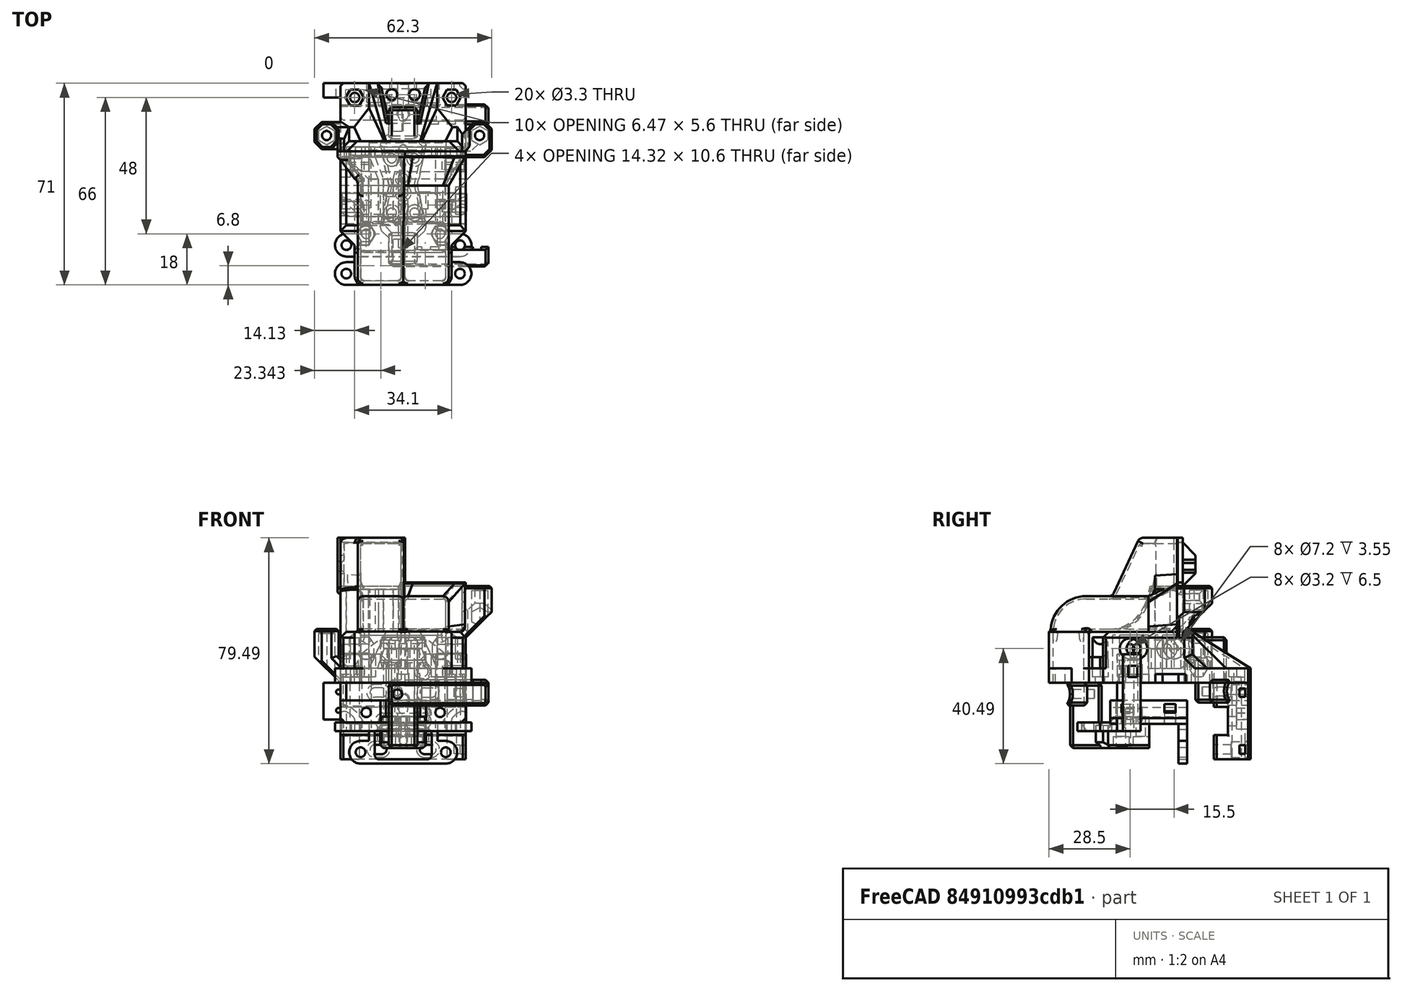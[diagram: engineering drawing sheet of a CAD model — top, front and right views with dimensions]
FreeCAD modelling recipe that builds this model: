
FCSTD DOCUMENT  (FreeCAD 0.19R24291 (Git))
Label: mounting-plate-dual-5015
License: Other
LicenseURL: GPL3
objects: Part::Box×16, Part::Cylinder×13, Part::MultiFuse×12, Part::Feature×11, Part::Cut×10, Part::Chamfer×3, Part::MultiCommon×1
note: 66 computed .brp shape members not serialized (recipe doc carries the construction recipe); baked Part::Feature solids carry a one-line shape summary decoded from their .brp

FEATURE [Part::Cylinder] Cylinder013
  Angle = 360
  AttacherType = Attacher::AttachEngine3D
  Height = 44
  Placement = pos=(21.5,6.5,13.5) rot=(0.707107,0,-0.707107;3.14159rad)
  Radius = 1.6
FEATURE [Part::Cylinder] Cylinder014
  Angle = 360
  AttacherType = Attacher::AttachEngine3D
  Height = 44
  Placement = pos=(-21.5,-6.5,13.5) rot=(0,1,0;1.5708rad)
  Radius = 1.6
FEATURE [Part::Cylinder] Cylinder015
  Angle = 360
  AttacherType = Attacher::AttachEngine3D
  Height = 4
  Placement = pos=(18.5,-6.5,13.5) rot=(0,1,0;1.5708rad)
  Radius = 3.6
FEATURE [Part::Cylinder] Cylinder016
  Angle = 360
  AttacherType = Attacher::AttachEngine3D
  Height = 4
  Placement = pos=(-18.5,6.5,13.5) rot=(0.707107,0,-0.707107;3.14159rad)
  Radius = 3.6
FEATURE [Part::Box] Box012  label="belt-slot"
  AttacherType = Attacher::AttachEngine3D
  Height = 10.2
  Length = 27
  Placement = pos=(-12,15.1,3.5) rot=(1,0,0;1.5708rad)
  Width = 16.7
FEATURE [Part::Box] Box013  label="belt-slot003"
  AttacherType = Attacher::AttachEngine3D
  Height = 10.2
  Length = 27
  Placement = pos=(-15,0.1,3.5) rot=(1,0,0;1.5708rad)
  Width = 16.7
FEATURE [Part::MultiFuse] Fusion001007010
  Placement = pos=(0,2.5,2) rot=(0,0,1;0rad)
  Shapes = -> [Cylinder015,Cylinder016,Cylinder013,Cylinder014]
FEATURE [Part::Box] Box022  label="Cube020"
  AttacherType = Attacher::AttachEngine3D
  Height = 3
  Length = 10
  Placement = pos=(13,4.9,3.5) rot=(0,0,1;0rad)
  Width = 8.2
FEATURE [Part::Box] Box023  label="Cube021"
  AttacherType = Attacher::AttachEngine3D
  Height = 3
  Length = 10
  Placement = pos=(-23,-8.1,3.5) rot=(0,0,1;0rad)
  Width = 8.2
FEATURE [Part::MultiFuse] Fusion001007011023
  Shapes = -> [Box023,Box022]
FEATURE [Part::Cylinder] Cylinder019
  Angle = 360
  AttacherType = Attacher::AttachEngine3D
  Height = 4
  Placement = pos=(-18.5,6.5,13.5) rot=(0.707107,0,-0.707107;3.14159rad)
  Radius = 3.6
FEATURE [Part::Box] Box024  label="belt-slot004"
  AttacherType = Attacher::AttachEngine3D
  Height = 10.2
  Length = 27
  Placement = pos=(-12,12.6,3.5) rot=(1,0,0;1.5708rad)
  Width = 16.7
FEATURE [Part::Box] Box025  label="belt-slot005"
  AttacherType = Attacher::AttachEngine3D
  Height = 10.2
  Length = 27
  Placement = pos=(-15,-2.4,3.5) rot=(1,0,0;1.5708rad)
  Width = 16.7
FEATURE [Part::Cylinder] Cylinder020
  Angle = 360
  AttacherType = Attacher::AttachEngine3D
  Height = 44
  Placement = pos=(21.5,6.5,13.5) rot=(0.707107,0,-0.707107;3.14159rad)
  Radius = 1.6
FEATURE [Part::Cylinder] Cylinder021
  Angle = 360
  AttacherType = Attacher::AttachEngine3D
  Height = 44
  Placement = pos=(-21.5,-6.5,13.5) rot=(0,1,0;1.5708rad)
  Radius = 1.6
FEATURE [Part::Cylinder] Cylinder022
  Angle = 360
  AttacherType = Attacher::AttachEngine3D
  Height = 4
  Placement = pos=(18.5,-6.5,13.5) rot=(0,1,0;1.5708rad)
  Radius = 3.6
FEATURE [Part::MultiFuse] Fusion001007011029
  Placement = pos=(0,0,2) rot=(0,0,1;0rad)
  Shapes = -> [Cylinder022,Cylinder019,Cylinder020,Cylinder021]
FEATURE [Part::Box] Box027  label="Cube023"
  AttacherType = Attacher::AttachEngine3D
  Height = 3
  Length = 10
  Placement = pos=(13,4.9,3.5) rot=(0,0,1;0rad)
  Width = 8.2
FEATURE [Part::Box] Box028  label="Cube024"
  AttacherType = Attacher::AttachEngine3D
  Height = 3
  Length = 10
  Placement = pos=(-23,-8.1,3.5) rot=(0,0,1;0rad)
  Width = 8.2
FEATURE [Part::MultiFuse] Fusion001007011032
  Placement = pos=(0,-2.5,0) rot=(0,0,1;0rad)
  Shapes = -> [Box028,Box027]
FEATURE [Part::MultiFuse] Fusion001007011055
  Shapes = -> [Box012,Box013]
FEATURE [Part::MultiFuse] Fusion001007011056
  Shapes = -> [Fusion001007011023,Fusion001007011055,Fusion001007010]
FEATURE [Part::MultiFuse] Fusion001007011058
  Shapes = -> [Box024,Box025]
FEATURE [Part::MultiFuse] Fusion001007011059
  Shapes = -> [Fusion001007011032,Fusion001007011058,Fusion001007011029]
FEATURE [Part::Feature] Chamfer005021077002006007019003032007005  label="dual-1515-origin"
  Placement = pos=(3.8e-15,31,3.5) rot=(0,0,1;3.14159rad)
  shape: bbox 62.38 x 71.58 x 51.08 mm, 481 faces (baked)
FEATURE [Part::Feature] Chamfer005021077002006007019003032007006  label="dual-1515-origin001"
  Placement = pos=(4e-15,31,3.5) rot=(0,0,1;3.14159rad)
  shape: bbox 62.38 x 71.58 x 51.08 mm, 481 faces (baked)
FEATURE [Part::Cut] Cut  label="2020-back-dual-5015"
  Base = -> Chamfer005021077002006007019003032007006
  Tool = -> Fusion001007011059
FEATURE [Part::Cut] Cut001  label="1515-back-dual-5015"
  Base = -> Chamfer005021077002006007019003032007005
  Tool = -> Fusion001007011056
FEATURE [Part::Box] Box  label="Cube"
  AttacherType = Attacher::AttachEngine3D
  Height = 15.38
  Length = 20.5
  Placement = pos=(0.28,10.29,22.07) rot=(0,0,1;0rad)
  Width = 10
FEATURE [Part::Box] Box029  label="Cube025"
  AttacherType = Attacher::AttachEngine3D
  Height = 15.38
  Length = 20.5
  Placement = pos=(-20.77,10.02,37.45) rot=(0,0,1;0rad)
  Width = 10
FEATURE [Part::Feature] Cut002  label="2020-back-dual-5016"
  shape: bbox 62.38 x 71.58 x 51.08 mm, 509 faces (baked)
FEATURE [Part::Feature] Cut001001  label="1515-back-dual-5016"
  shape: bbox 62.38 x 71.58 x 51.08 mm, 514 faces (baked)
FEATURE [Part::Box] Box030  label="Cube026"
  AttacherType = Attacher::AttachEngine3D
  Height = 15.38
  Length = 20.5
  Placement = pos=(-20.77,10.02,37.45) rot=(0,0,1;0rad)
  Width = 10
FEATURE [Part::Box] Box031  label="Cube027"
  AttacherType = Attacher::AttachEngine3D
  Height = 15.38
  Length = 20.5
  Placement = pos=(0.27,10.29,22.07) rot=(0,0,1;0rad)
  Width = 10
FEATURE [Part::Cut] Cut001002
  Base = -> Cut002
  Tool = -> Box031
FEATURE [Part::Cut] Cut001003  label="2020-back-dual-5015-wider"
  Base = -> Cut001002
  Tool = -> Box030
FEATURE [Part::Cut] Cut001004
  Base = -> Cut001001
  Tool = -> Box029
FEATURE [Part::Cut] Cut001005  label="1515-back-dual-5015-wider"
  Base = -> Cut001004
  Tool = -> Box
FEATURE [Part::Feature] Pocket011001
  Placement = pos=(0,-10,-10) rot=(1,0,0;4.71239rad)
  shape: bbox 50.05 x 13 x 27 mm, 100 faces (baked)
FEATURE [Part::Feature] Chamfer001002001  label="extruder-cable-support"
  Placement = pos=(1.5e-15,-0.3,19.5) rot=(0,-1,0;3.14159rad)
  shape: bbox 38.38 x 29.43 x 11.83 mm, 84 faces (baked)
FEATURE [Part::Feature] Cut001005001  label="1515-back-dual-5015-wider001"
  shape: bbox 62.38 x 71.58 x 51.08 mm, 530 faces (baked)
FEATURE [Part::Box] Box032  label="Cube028"
  AttacherType = Attacher::AttachEngine3D
  Height = 10
  Length = 39
  Placement = pos=(-5.9,21.5,10.4) rot=(0,0,1;0rad)
  Width = 10
FEATURE [Part::Feature] Chamfer005021077002006007019003032007007  label="extruder-cable-support001"
  Placement = pos=(2e-15,-0.3,19.5) rot=(0,1,0;3.14159rad)
  shape: bbox 38.38 x 29.43 x 11.83 mm, 84 faces (baked)
FEATURE [Part::Box] Box033  label="Cube029"
  AttacherType = Attacher::AttachEngine3D
  Height = 10
  Length = 39
  Placement = pos=(-5.9,21.5,10.4) rot=(0,0,1;0rad)
  Width = 10
FEATURE [Part::Cut] Cut001005002
  Base = -> Chamfer005021077002006007019003032007007
  Tool = -> Box032
FEATURE [Part::MultiCommon] Common
  Placement = pos=(0,0,-15) rot=(0,0,1;0rad)
  Shapes = -> [Chamfer001002001,Box033]
FEATURE [Part::Box] Box034  label="Cube030"
  AttacherType = Attacher::AttachEngine3D
  Height = 23
  Length = 10
  Placement = pos=(-5,16.5,-3.5) rot=(0,0,1;0rad)
  Width = 11
FEATURE [Part::Chamfer] Chamfer
  Base = -> Box034
  Edges = 12 edges r=1: [Edge1,Edge2,Edge3,Edge4,Edge5,Edge6,Edge7,Edge8,Edge9,Edge10,Edge11,Edge12]
FEATURE [Part::MultiFuse] Fusion
  Shapes = -> [Cut001005002,Chamfer,Common]
FEATURE [Part::Cylinder] Cylinder
  Angle = 360
  AttacherType = Attacher::AttachEngine3D
  Height = 10
  Placement = pos=(-2,19,0.5) rot=(1,0,0;4.71239rad)
  Radius = 1.6
FEATURE [Part::Cut] Cut001005003
  Base = -> Fusion
  Tool = -> Cylinder
FEATURE [Part::Feature] Cut001005003001001
  Placement = pos=(0,0,0) rot=(1,0,0;3.14159rad)
  shape: bbox 38.38 x 29.43 x 23.83 mm, 95 faces (baked)
FEATURE [Part::Cylinder] Cylinder071
  Angle = 360
  AttacherType = Attacher::AttachEngine3D
  Height = 1
  Placement = pos=(7,-7.5,-3.29) rot=(0,0,1;0rad)
  Radius = 3
FEATURE [Part::Cylinder] Cylinder072
  Angle = 360
  AttacherType = Attacher::AttachEngine3D
  Height = 1
  Placement = pos=(7,7.5,-3.29) rot=(0,0,1;0rad)
  Radius = 3
FEATURE [Part::MultiFuse] Fusion036012039011002025018010027013001002002001002001029004001010001015008003008002
  Shapes = -> [Cylinder072,Cylinder071]
FEATURE [Part::Chamfer] Chamfer005021077002006007019003032012
  Base = -> Fusion036012039011002025018010027013001002002001002001029004001010001015008003008002
  Edges = 2 edges r=0.5: [Edge1,Edge4]
  Placement = pos=(0,0.04,0) rot=(0,0,1;0rad)
FEATURE [Part::Box] Box050  label="Cube045"
  AttacherType = Attacher::AttachEngine3D
  Height = 10
  Length = 5
  Placement = pos=(-7,-10.87,-3.79) rot=(0,0,1;0rad)
  Width = 22
FEATURE [Part::Chamfer] Chamfer005021077002006007019003032013
  Base = -> Box050
  Edges = 4 edges r=1: [Edge4,Edge8,Edge9,Edge11]
FEATURE [Part::Feature] Part__Feature112001134  label="bottom_mgn12_short_duct001"
  Placement = pos=(0.00577366,-13.4565,-6.88873) rot=(0,0,1;0rad)
  shape: bbox 44.1 x 27 x 22.2 mm, 66 faces (baked)
FEATURE [Part::Cylinder] Cylinder069
  Angle = 360
  AttacherType = Attacher::AttachEngine3D
  Height = 6
  Placement = pos=(7,7.5,-3.29) rot=(0,0,1;0rad)
  Radius = 1.8
FEATURE [Part::Cylinder] Cylinder070
  Angle = 360
  AttacherType = Attacher::AttachEngine3D
  Height = 6
  Placement = pos=(7,-7.5,-3.29) rot=(0,0,1;0rad)
  Radius = 1.8
FEATURE [Part::MultiFuse] Fusion036012039011002025018010027013001002002001002001029004001010001015008003008003
  Placement = pos=(0,0,-5) rot=(0,0,1;0rad)
  Shapes = -> [Cylinder070,Cylinder069]
FEATURE [Part::Feature] Part__Feature  label="5015_2_Mod_3_Hinterteil_V2.0"
  Placement = pos=(0,-2.41,41.01) rot=(0,0,1;0rad)
  shape: bbox 48 x 27 x 22.2 mm, 56 faces (baked)
FEATURE [Part::MultiFuse] Fusion036012039011002025018010027013001002002001002001029004001010001015008003008004
  Shapes = -> [Part__Feature,Chamfer005021077002006007019003032012]
FEATURE [Part::Cut] Cut001005003001002
  Base = -> Fusion036012039011002025018010027013001002002001002001029004001010001015008003008004
  Tool = -> Chamfer005021077002006007019003032013
FEATURE [Part::Cut] Cut001005003001003
  Base = -> Cut001005003001002
  Placement = pos=(0,0,0) rot=(1,0,0;4.71239rad)
  Tool = -> Fusion036012039011002025018010027013001002002001002001029004001010001015008003008003
